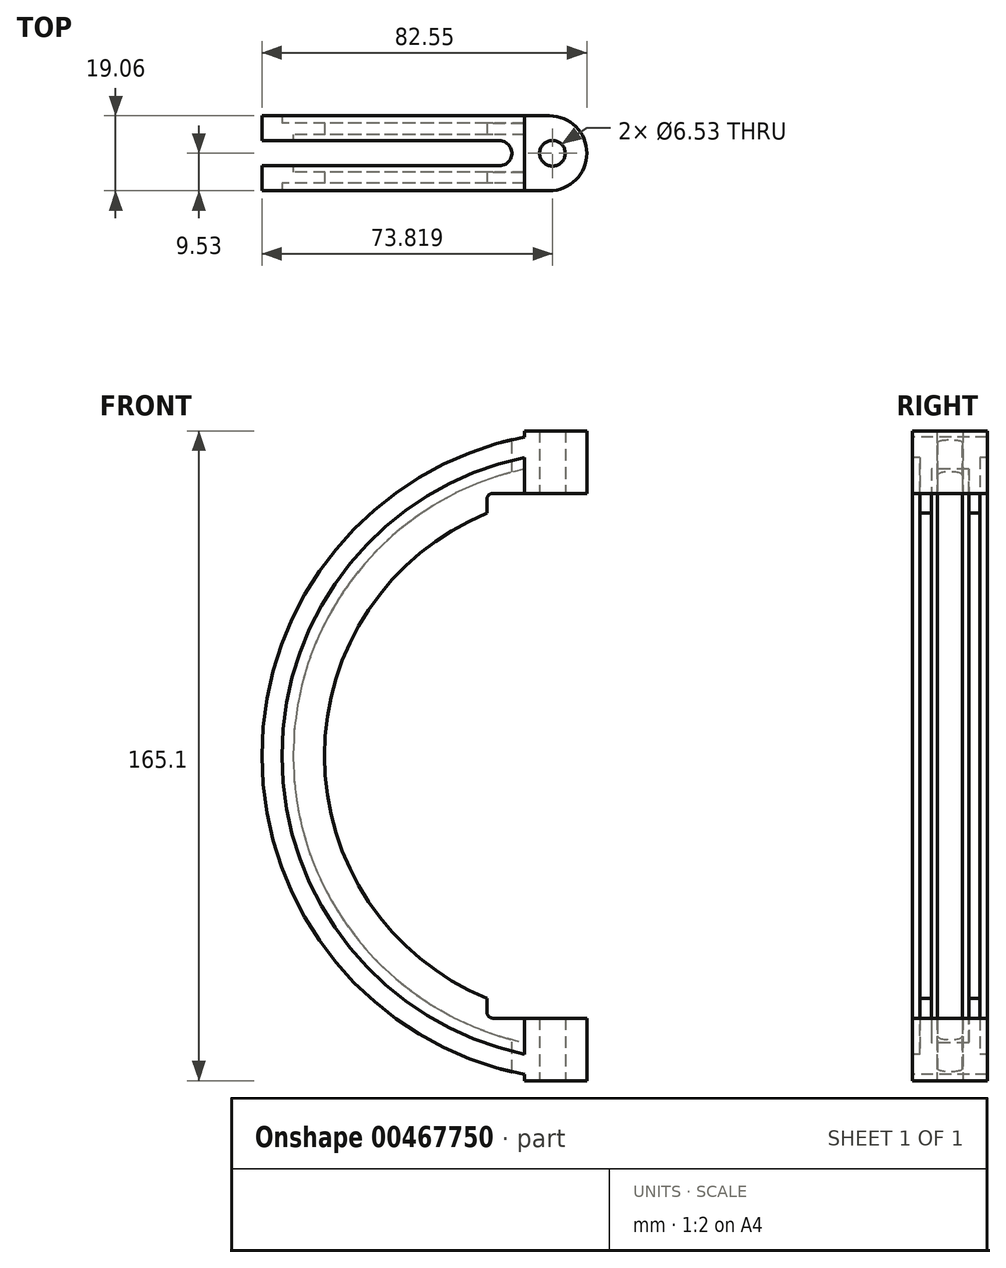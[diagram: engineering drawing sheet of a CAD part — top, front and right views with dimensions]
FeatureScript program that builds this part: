
annotation { "Feature Type Name" : "Feature", "Feature Type Description" : "" }
export const myFeature = defineFeature(function(context is Context, id is Id, definition is map)
    precondition{}
    {
        {
            var Q0;
            Q0=qCreatedBy(makeId("Front.planeOp"),FACE);
            var sketch = newSketch(context, id + "F0", { "sketchPlane" : qUnion([Q0]), "disableImprinting" : false});
            skArc(sketch, "E0", {"start": v(0, 76.2) * mm, "mid": v(-76.2, 0) * mm, "end": v(0, -76.2) * mm});
            skSolve(sketch);
        }
        {
            var Q0;
            Q0=qCreatedBy(makeId("Right.planeOp"),FACE);
            var sketch = newSketch(context, id + "F1", { "sketchPlane" : qUnion([Q0]), "disableImprinting" : false});
            skLineSegment(sketch, "E1", {"start": v(0, 0) * mm, "end": v(0, 114.7) * mm, "construction": true});
            skLineSegment(sketch, "E2", {"start": v(0, 82.55) * mm, "end": v(9.52, 82.55) * mm});
            skLineSegment(sketch, "E3", {"start": v(9.52, 82.55) * mm, "end": v(9.52, 77.47) * mm});
            skLineSegment(sketch, "E4", {"start": v(9.52, 77.47) * mm, "end": v(7.62, 77.47) * mm});
            skLineSegment(sketch, "E5", {"start": v(7.62, 77.47) * mm, "end": v(7.62, 66.67) * mm});
            skLineSegment(sketch, "E6", {"start": v(4.76, 66.67) * mm, "end": v(7.62, 66.67) * mm});
            skLineSegment(sketch, "E7", {"start": v(4.76, 74.61) * mm, "end": v(4.76, 66.67) * mm});
            skLineSegment(sketch, "E8", {"start": v(4.76, 74.61) * mm, "end": v(0, 74.61) * mm});
            skLineSegment(sketch, "E9.MirrorCS", {"start": v(0, 82.55) * mm, "end": v(-9.52, 82.55) * mm});
            skLineSegment(sketch, "E10.MirrorCS", {"start": v(-9.52, 82.55) * mm, "end": v(-9.52, 77.47) * mm});
            skLineSegment(sketch, "E11.MirrorCS", {"start": v(-9.52, 77.47) * mm, "end": v(-7.62, 77.47) * mm});
            skLineSegment(sketch, "E12.MirrorCS", {"start": v(-7.62, 77.47) * mm, "end": v(-7.62, 66.67) * mm});
            skLineSegment(sketch, "E13.MirrorCS", {"start": v(-4.76, 66.67) * mm, "end": v(-7.62, 66.67) * mm});
            skLineSegment(sketch, "E14.MirrorCS", {"start": v(-4.76, 74.61) * mm, "end": v(-4.76, 66.67) * mm});
            skLineSegment(sketch, "E15.MirrorCS", {"start": v(-4.76, 74.61) * mm, "end": v(0, 74.61) * mm});
            skSolve(sketch);
        }
        {
            var Q0;
            Q0=makeQuery(id+"F1.imprint","IMPRINT",FACE,{"disambiguationData":[TD([[makeQuery(id+"F1.imprint","IMPRINT",EDGE,{"derivedFrom":sQuery(id+"F1.wireOp",EDGE,"E2")}),-1.0]])]});
            var Q1;
            Q1=sQuery(id+"F0.wireOp",EDGE,"E0");
            sweep(context, id + "F2", {"profiles" : qUnion([Q0]), "path" : qUnion([Q1])});
        }
        {
            var Q0;
            Q0=makeQuery(id+"F2.opSweep","CAP_FACE",FACE,{"disambiguationData":[OSD([sQuery(id+"F0.wireOp",VERTEX,"E0.start"),sQuery(id+"F1.wireOp",EDGE,"E2"),sQuery(id+"F1.wireOp",EDGE,"E3"),sQuery(id+"F1.wireOp",EDGE,"E4"),sQuery(id+"F1.wireOp",EDGE,"E5"),sQuery(id+"F1.wireOp",EDGE,"E6"),sQuery(id+"F1.wireOp",EDGE,"E7"),sQuery(id+"F1.wireOp",EDGE,"E8"),sQuery(id+"F1.wireOp",EDGE,"d806f4fd-4342-4ff4-a3be-09678fabba640.MirrorCS"),sQuery(id+"F1.wireOp",EDGE,"a1c926de-faaa-42f6-8a03-f3addf501b060.MirrorCS"),sQuery(id+"F1.wireOp",EDGE,"9f7291a6-9b9e-40e9-9f87-0f9520c4ef080.MirrorCS"),sQuery(id+"F1.wireOp",EDGE,"5772085e-4ba6-4ca9-853a-f417a23b673f0.MirrorCS"),sQuery(id+"F1.wireOp",EDGE,"2e6904e3-8ce9-415a-846b-c01eafea8ad50.MirrorCS"),sQuery(id+"F1.wireOp",EDGE,"4e80b01c-79fc-4a74-85bd-2d8c2588cd3a0.MirrorCS"),sQuery(id+"F1.wireOp",EDGE,"3e42f510-c3c0-4e1d-9553-73f1ae95d8190.MirrorCS")])],"isStart":true});
            var sketch = newSketch(context, id + "F3", { "sketchPlane" : qUnion([Q0])});
            skLineSegment(sketch, "E16.bottom", {"start": v(9.52, 82.55) * mm, "end": v(-9.52, 82.55) * mm});
            skLineSegment(sketch, "E16.top", {"start": v(9.53, 66.67) * mm, "end": v(-9.53, 66.67) * mm});
            skLineSegment(sketch, "E16.left", {"start": v(9.52, 82.55) * mm, "end": v(9.52, 66.67) * mm});
            skLineSegment(sketch, "E16.right", {"start": v(-9.52, 82.55) * mm, "end": v(-9.52, 66.67) * mm});
            skLineSegment(sketch, "E17.bottom", {"start": v(9.52, -82.55) * mm, "end": v(-9.52, -82.55) * mm});
            skLineSegment(sketch, "E17.top", {"start": v(9.52, -66.67) * mm, "end": v(-9.52, -66.67) * mm});
            skLineSegment(sketch, "E17.left", {"start": v(9.52, -82.55) * mm, "end": v(9.52, -66.67) * mm});
            skLineSegment(sketch, "E17.right", {"start": v(-9.52, -82.55) * mm, "end": v(-9.52, -66.67) * mm});
            skSolve(sketch);
        }
        {
            var Q0;
            Q0=qSketchRegion(id+"F3",true);
            extrude(context, id + "F4", {"entities" : qUnion([Q0]), "operationType" : NewBodyOperationType.ADD, "oppositeDirection" : true, "depth" : 15.88 * mm});
        }
        {
            var Q0;
            Q0=makeQuery(id+"F4.opExtrude","SWEPT_FACE",FACE,{"disambiguationData":[OSD([sQuery(id+"F3.wireOp",EDGE,"E16.bottom")])]});
            var sketch = newSketch(context, id + "F5", { "sketchPlane" : qUnion([Q0])});
            skPoint(sketch, "E18", {"position": v(-8.73, 0) * mm});
            skSolve(sketch);
        }
        {
            var Q0;
            Q0=sQuery(id+"F5.wireOp",VERTEX,"E18");
            var Q1;
            Q1=makeQuery(id+"F2.opSweep","SWEPT_BODY",BODY,{"disambiguationData":[OSD([sQuery(id+"F0.wireOp",EDGE,"E0"),sQuery(id+"F1.wireOp",EDGE,"E2"),sQuery(id+"F1.wireOp",EDGE,"E3"),sQuery(id+"F1.wireOp",EDGE,"E4"),sQuery(id+"F1.wireOp",EDGE,"E5"),sQuery(id+"F1.wireOp",EDGE,"E6"),sQuery(id+"F1.wireOp",EDGE,"E7"),sQuery(id+"F1.wireOp",EDGE,"E8"),sQuery(id+"F1.wireOp",EDGE,"d806f4fd-4342-4ff4-a3be-09678fabba640.MirrorCS"),sQuery(id+"F1.wireOp",EDGE,"a1c926de-faaa-42f6-8a03-f3addf501b060.MirrorCS"),sQuery(id+"F1.wireOp",EDGE,"9f7291a6-9b9e-40e9-9f87-0f9520c4ef080.MirrorCS"),sQuery(id+"F1.wireOp",EDGE,"5772085e-4ba6-4ca9-853a-f417a23b673f0.MirrorCS"),sQuery(id+"F1.wireOp",EDGE,"2e6904e3-8ce9-415a-846b-c01eafea8ad50.MirrorCS"),sQuery(id+"F1.wireOp",EDGE,"4e80b01c-79fc-4a74-85bd-2d8c2588cd3a0.MirrorCS"),sQuery(id+"F1.wireOp",EDGE,"3e42f510-c3c0-4e1d-9553-73f1ae95d8190.MirrorCS")])]});
            hole(context, id + "F6", {"style" : HoleStyle.SIMPLE, "endStyle" : HoleEndStyle.THROUGH, "standardTappedOrClearance" : lookupTablePath({ "standard" : "ANSI", "fit" : "Close", "size" : "1/4", "type" : "Clearance" }), "standardBlindInLast" : lookupTablePath({ "fit" : "Close", "standard" : "ANSI", "size" : "1/4", "type" : "Clearance" }), "holeDiameter" : 6.53 * mm, "isTappedThrough" : true, "tappedDepth" : 12.7 * mm, "tapClearance" : 3, "locations" : qUnion([Q0]), "scope" : qUnion([Q1]), "startStyle" : HoleStartStyle.SKETCH});
        }
        {
            var Q0;
            Q0=makeQuery(id+"F4.opExtrude","SWEPT_FACE",FACE,{"disambiguationData":[OSD([sQuery(id+"F3.wireOp",EDGE,"E16.bottom")])]});
            var sketch = newSketch(context, id + "F7", { "sketchPlane" : qUnion([Q0])});
            skLineSegment(sketch, "E19.bottom", {"start": v(-114.3, 3.17) * mm, "end": v(-22.23, 3.18) * mm});
            skLineSegment(sketch, "E19.top", {"start": v(-114.3, -3.17) * mm, "end": v(-22.23, -3.17) * mm});
            skLineSegment(sketch, "E19.left", {"start": v(-114.3, 3.18) * mm, "end": v(-114.3, -3.18) * mm});
            skLineSegment(sketch, "E19.right", {"start": v(-19.05, 0) * mm, "end": v(-19.05, 0) * mm});
            skLineSegment(sketch, "E20", {"start": v(0, 0) * mm, "end": v(-165.93, 0) * mm, "construction": true});
            skPoint(sketch, "E21.visualSharp", {"position": v(-19.05, 3.18) * mm});
            skArc(sketch, "E21.filletArc", {"start": v(-19.05, 0) * mm, "mid": v(-19.98, 2.25) * mm, "end": v(-22.23, 3.18) * mm});
            skPoint(sketch, "E22.visualSharp", {"position": v(-19.05, -3.17) * mm});
            skArc(sketch, "E22.filletArc", {"start": v(-22.23, -3.18) * mm, "mid": v(-19.98, -2.25) * mm, "end": v(-19.05, 0) * mm});
            skSolve(sketch);
        }
        {
            var Q0;
            Q0 = qSketchRegion(id + "F7", true);
            extrude(context, id + "F8", {"entities" : qUnion([Q0]), "operationType" : NewBodyOperationType.REMOVE, "endBound" : BoundingType.THROUGH_ALL, "oppositeDirection" : true, "depth" : 25.4 * mm});
        }
        {
            var Q0;
            Q0=makeQuery(id+"F4.boolean.opBoolean","MERGE",EDGE,{"derivedFrom":[makeQuery(id+"F2.opSweep","CAP_EDGE",EDGE,{"disambiguationData":[OSD([sQuery(id+"F0.wireOp",VERTEX,"E0.start"),sQuery(id+"F1.wireOp",EDGE,"E10.MirrorCS")])],"isStart":true}),makeQuery(id+"F4.opExtrude","CAP_EDGE",EDGE,{"disambiguationData":[OSD([sQuery(id+"F3.wireOp",EDGE,"E16.right")])],"isStart":true})]});
            var Q1;
            Q1=makeQuery(id+"F4.boolean.opBoolean","MERGE",EDGE,{"derivedFrom":[makeQuery(id+"F2.opSweep","CAP_EDGE",EDGE,{"disambiguationData":[OSD([sQuery(id+"F0.wireOp",VERTEX,"E0.start"),sQuery(id+"F1.wireOp",EDGE,"E3")])],"isStart":true}),makeQuery(id+"F4.opExtrude","CAP_EDGE",EDGE,{"disambiguationData":[OSD([sQuery(id+"F3.wireOp",EDGE,"E16.left")])],"isStart":true})]});
            var Q2;
            Q2=makeQuery(id+"F4.boolean.opBoolean","MERGE",EDGE,{"derivedFrom":[makeQuery(id+"F2.opSweep","CAP_EDGE",EDGE,{"disambiguationData":[OSD([sQuery(id+"F0.wireOp",VERTEX,"E0.end"),sQuery(id+"F1.wireOp",EDGE,"E10.MirrorCS")])],"isStart":false}),makeQuery(id+"F4.opExtrude","CAP_EDGE",EDGE,{"disambiguationData":[OSD([sQuery(id+"F3.wireOp",EDGE,"E17.right")])],"isStart":true})]});
            var Q3;
            Q3=makeQuery(id+"F4.boolean.opBoolean","MERGE",EDGE,{"derivedFrom":[makeQuery(id+"F2.opSweep","CAP_EDGE",EDGE,{"disambiguationData":[OSD([sQuery(id+"F0.wireOp",VERTEX,"E0.end"),sQuery(id+"F1.wireOp",EDGE,"E3")])],"isStart":false}),makeQuery(id+"F4.opExtrude","CAP_EDGE",EDGE,{"disambiguationData":[OSD([sQuery(id+"F3.wireOp",EDGE,"E17.left")])],"isStart":true})]});
            fillet(context, id + "F9", {"entities" : qUnion([Q0, Q1, Q2, Q3]), "radius" : 9.52 * mm, "tangentPropagation" : true, "allowEdgeOverflow" : false});
        }
        {
            var Q0;
            Q0=makeQuery(id+"F2.opSweep","SWEPT_FACE",FACE,{"disambiguationData":[OSD([sQuery(id+"F0.wireOp",EDGE,"E0"),sQuery(id+"F1.wireOp",EDGE,"E12.MirrorCS")])]});
            var sketch = newSketch(context, id + "F10", { "sketchPlane" : qUnion([Q0]), "disableImprinting" : false});
            skLineSegment(sketch, "E23.bottom", {"start": v(0, 66.67) * mm, "end": v(-23.81, 66.67) * mm});
            skLineSegment(sketch, "E23.top", {"start": v(0, 60.32) * mm, "end": v(-25.4, 60.32) * mm});
            skLineSegment(sketch, "E23.left", {"start": v(0, 66.67) * mm, "end": v(0, 60.32) * mm});
            skLineSegment(sketch, "E23.right", {"start": v(-25.4, 65.09) * mm, "end": v(-25.4, 60.32) * mm});
            skPoint(sketch, "E24.visualSharp", {"position": v(-25.4, 66.67) * mm});
            skArc(sketch, "E24.filletArc", {"start": v(-23.81, 66.67) * mm, "mid": v(-24.94, 66.21) * mm, "end": v(-25.4, 65.09) * mm});
            skLineSegment(sketch, "E25.bottom", {"start": v(0, -66.68) * mm, "end": v(-23.81, -66.68) * mm});
            skLineSegment(sketch, "E25.top", {"start": v(0, -60.33) * mm, "end": v(-25.4, -60.33) * mm});
            skLineSegment(sketch, "E25.left", {"start": v(0, -66.68) * mm, "end": v(0, -60.33) * mm});
            skLineSegment(sketch, "E25.right", {"start": v(-25.4, -65.09) * mm, "end": v(-25.4, -60.33) * mm});
            skPoint(sketch, "E26.visualSharp", {"position": v(-25.4, -66.68) * mm});
            skArc(sketch, "E26.filletArc", {"start": v(-25.4, -65.09) * mm, "mid": v(-24.94, -66.21) * mm, "end": v(-23.81, -66.68) * mm});
            skSolve(sketch);
        }
        {
            var Q0;
            Q0 = qSketchRegion(id + "F10", true);
            extrude(context, id + "F11", {"entities" : qUnion([Q0]), "operationType" : NewBodyOperationType.REMOVE, "endBound" : BoundingType.THROUGH_ALL, "oppositeDirection" : true, "depth" : 25.4 * mm});
        }
    });
